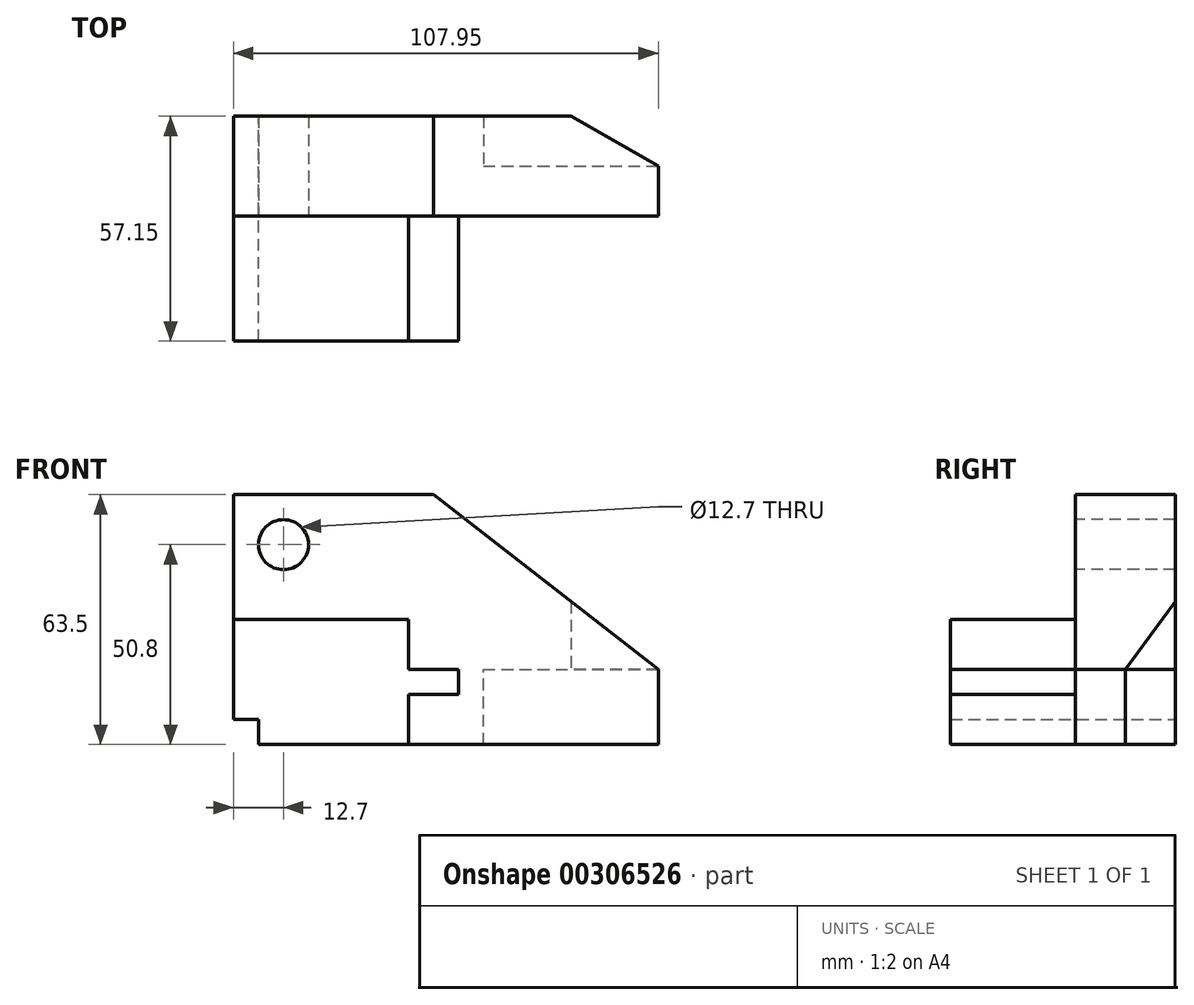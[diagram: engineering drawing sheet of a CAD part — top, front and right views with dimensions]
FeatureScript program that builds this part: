
annotation { "Feature Type Name" : "Feature", "Feature Type Description" : "" }
export const myFeature = defineFeature(function(context is Context, id is Id, definition is map)
    precondition{}
    {
        {
            var Q0;
            Q0=qCreatedBy(makeId("Front.planeOp"),FACE);
            var sketch = newSketch(context, id + "F0", { "sketchPlane" : qUnion([Q0])});
            skLineSegment(sketch, "E0.bottom", {"start": v(6.35, 0) * mm, "end": v(44.45, 0) * mm});
            skLineSegment(sketch, "E0.top", {"start": v(0, 31.75) * mm, "end": v(44.45, 31.75) * mm});
            skLineSegment(sketch, "E0.left", {"start": v(0, 6.35) * mm, "end": v(0, 31.75) * mm});
            skLineSegment(sketch, "E0.right", {"start": v(44.45, 0) * mm, "end": v(44.45, 12.7) * mm});
            skLineSegment(sketch, "E1.top", {"start": v(0, 6.35) * mm, "end": v(6.35, 6.35) * mm});
            skLineSegment(sketch, "E1.right", {"start": v(6.35, 0) * mm, "end": v(6.35, 6.35) * mm});
            skLineSegment(sketch, "E2.bottom", {"start": v(57.15, 19.05) * mm, "end": v(44.45, 19.05) * mm});
            skLineSegment(sketch, "E2.top", {"start": v(57.15, 12.7) * mm, "end": v(44.45, 12.7) * mm});
            skLineSegment(sketch, "E2.left", {"start": v(57.15, 19.05) * mm, "end": v(57.15, 12.7) * mm});
            skLineSegment(sketch, "E3.trimOffspring", {"start": v(44.45, 19.05) * mm, "end": v(44.45, 31.75) * mm});
            skSolve(sketch);
        }
        {
            var Q0;
            Q0 = qSketchRegion(id + "F0", true);
            extrude(context, id + "F1", {"entities" : qUnion([Q0]), "depth" : 31.75 * mm});
        }
        {
            var Q0;
            Q0=makeQuery(id+"F1.opExtrude","CAP_FACE",FACE,{"disambiguationData":[OSD([sQuery(id+"F0.wireOp",EDGE,"E0.bottom"),sQuery(id+"F0.wireOp",EDGE,"E0.top"),sQuery(id+"F0.wireOp",EDGE,"E0.left"),sQuery(id+"F0.wireOp",EDGE,"E0.right"),sQuery(id+"F0.wireOp",EDGE,"E1.top"),sQuery(id+"F0.wireOp",EDGE,"E1.right"),sQuery(id+"F0.wireOp",EDGE,"E2.bottom"),sQuery(id+"F0.wireOp",EDGE,"E2.top"),sQuery(id+"F0.wireOp",EDGE,"E2.left"),sQuery(id+"F0.wireOp",EDGE,"E3.trimOffspring")])],"isStart":true});
            var sketch = newSketch(context, id + "F2", { "sketchPlane" : qUnion([Q0])});
            skLineSegment(sketch, "E4.bottom", {"start": v(0, 0) * mm, "end": v(-107.95, 0) * mm});
            skLineSegment(sketch, "E4.top", {"start": v(0, 63.5) * mm, "end": v(-50.8, 63.5) * mm});
            skLineSegment(sketch, "E4.left", {"start": v(0, 0) * mm, "end": v(0, 63.5) * mm});
            skLineSegment(sketch, "E4.right", {"start": v(-107.95, 0) * mm, "end": v(-107.95, 19.05) * mm});
            skPoint(sketch, "E5", {"position": v(-107.95, 19.05) * mm});
            skPoint(sketch, "E6", {"position": v(-50.8, 63.5) * mm});
            skLineSegment(sketch, "E7", {"start": v(-107.95, 19.05) * mm, "end": v(-50.8, 63.5) * mm});
            skSolve(sketch);
        }
        {
            var Q0;
            {var subQ4=sQuery(id+"F2.wireOp",EDGE,"E4.top");Q0=makeQuery(id+"F2.imprint","IMPRINT",FACE,{"disambiguationData":[TD([[makeQuery(id+"F2.imprint","IMPRINT",EDGE,{"derivedFrom":subQ4}),1.0]])]});}
            var Q1;
            {var subQ0=makeQuery(id+"F1.opExtrude","CAP_EDGE",EDGE,{"disambiguationData":[OSD([sQuery(id+"F0.wireOp",EDGE,"E0.top")])],"isStart":true});Q1=makeQuery(id+"F2.imprint","IMPRINT",FACE,{"disambiguationData":[TD([[makeQuery(id+"F2.imprint","IMPRINT",EDGE,{"derivedFrom":subQ0}),1.0]])]});}
            extrude(context, id + "F3", {"entities" : qUnion([Q0, Q1]), "operationType" : NewBodyOperationType.ADD, "depth" : 25.4 * mm});
        }
        {
            var Q0;
            Q0=makeQuery(id+"F3.opExtrude","CAP_FACE",FACE,{"disambiguationData":[OSD([sQuery(id+"F0.wireOp",EDGE,"E1.top"),sQuery(id+"F0.wireOp",EDGE,"E1.right"),sQuery(id+"F2.wireOp",EDGE,"E4.bottom"),sQuery(id+"F2.wireOp",EDGE,"E4.top"),sQuery(id+"F2.wireOp",EDGE,"E4.left"),sQuery(id+"F2.wireOp",EDGE,"E4.right"),sQuery(id+"F2.wireOp",EDGE,"E7")])],"isStart":true});
            var sketch = newSketch(context, id + "F4", { "sketchPlane" : qUnion([Q0])});
            skCircle(sketch, "E8", {"center": v(12.7, 50.8) * mm, "radius": 6.35 * mm});
            skSolve(sketch);
        }
        {
            var Q0;
            Q0 = qSketchRegion(id + "F4", true);
            extrude(context, id + "F5", {"entities" : qUnion([Q0]), "operationType" : NewBodyOperationType.REMOVE, "endBound" : BoundingType.UP_TO_NEXT, "oppositeDirection" : true, "depth" : 25.4 * mm});
        }
        {
            var Q0;
            Q0=makeQuery(id+"F3.opExtrude","SWEPT_FACE",FACE,{"disambiguationData":[OSD([sQuery(id+"F2.wireOp",EDGE,"E4.right")])]});
            var sketch = newSketch(context, id + "F6", { "sketchPlane" : qUnion([Q0])});
            skLineSegment(sketch, "E9", {"start": v(12.7, 19.05) * mm, "end": v(12.7, 0) * mm});
            skSolve(sketch);
        }
        {
            var Q0;
            {var subQ0=sQuery(id+"F6.wireOp",EDGE,"E9");Q0=makeQuery(id+"F6.imprint","IMPRINT",FACE,{"disambiguationData":[TD([[makeQuery(id+"F6.imprint","IMPRINT",EDGE,{"derivedFrom":subQ0}),1.0]])]});}
            extrude(context, id + "F7", {"entities" : qUnion([Q0]), "operationType" : NewBodyOperationType.REMOVE, "oppositeDirection" : true, "depth" : 44.45 * mm});
        }
        {
            var Q0;
            Q0=makeQuery(id+"F7.boolean.opBoolean","COPY",FACE,{"derivedFrom":makeQuery(id+"F7.opExtrude","SWEPT_FACE",FACE,{"disambiguationData":[OSD([sQuery(id+"F2.wireOp",EDGE,"E4.right"),sQuery(id+"F2.wireOp",EDGE,"E7")])]})});
            var sketch = newSketch(context, id + "F8", { "sketchPlane" : qUnion([Q0])});
            skLineSegment(sketch, "E10", {"start": v(107.95, -12.7) * mm, "end": v(85.72, -25.4) * mm});
            skSolve(sketch);
        }
        {
            var Q0;
            {var subQ0=sQuery(id+"F8.wireOp",EDGE,"E10");Q0=makeQuery(id+"F8.imprint","IMPRINT",FACE,{"disambiguationData":[TD([[makeQuery(id+"F8.imprint","IMPRINT",EDGE,{"derivedFrom":subQ0}),1.0]])]});}
            extrude(context, id + "F9", {"entities" : qUnion([Q0]), "operationType" : NewBodyOperationType.REMOVE, "endBound" : BoundingType.THROUGH_ALL, "oppositeDirection" : true, "depth" : 25.4 * mm});
        }
    });
